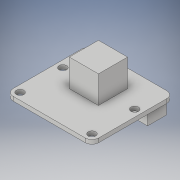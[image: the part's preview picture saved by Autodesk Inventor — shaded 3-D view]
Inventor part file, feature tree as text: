
AUTODESK INVENTOR PART (.ipt)
format: ipt  version: 2019 (Build 230136000, 136)  size: 151,040 bytes
history: native  units: mm
features: extrude x3, sketch x3
ambient origin geometry x8: Origin, YZ Plane, XZ Plane, XY Plane, X Axis, Y Axis, Z Axis, Center Point
bodies: Solid1 (feature_tree)
feature tree (6):
  extrude  "Extrusion1"  Depth=23.862mm
  extrude  "Extrusion2"  Depth=2.0mm
  extrude  "Extrusion3"  Depth=2.0mm
  sketch  "Sketch1"  dims[d0=25.0mm d1=23.862mm]
  sketch  "Sketch2"  dims[d2=2.0mm d3=2.0mm]
  sketch  "Sketch3"  dims[d4=14.5mm d5=2.0mm d6=2.0mm d7=2.2mm d8=2.2mm d9=2.2mm d10=2.2mm d11=1.2mm d12=0.0mm d13=8.5mm d14=8.5mm d15=12.5mm d16=9.462mm d17=8.0mm d18=0.0mm d19=20.8mm d20=5.5mm d21=5.0mm d22=0.0mm]
